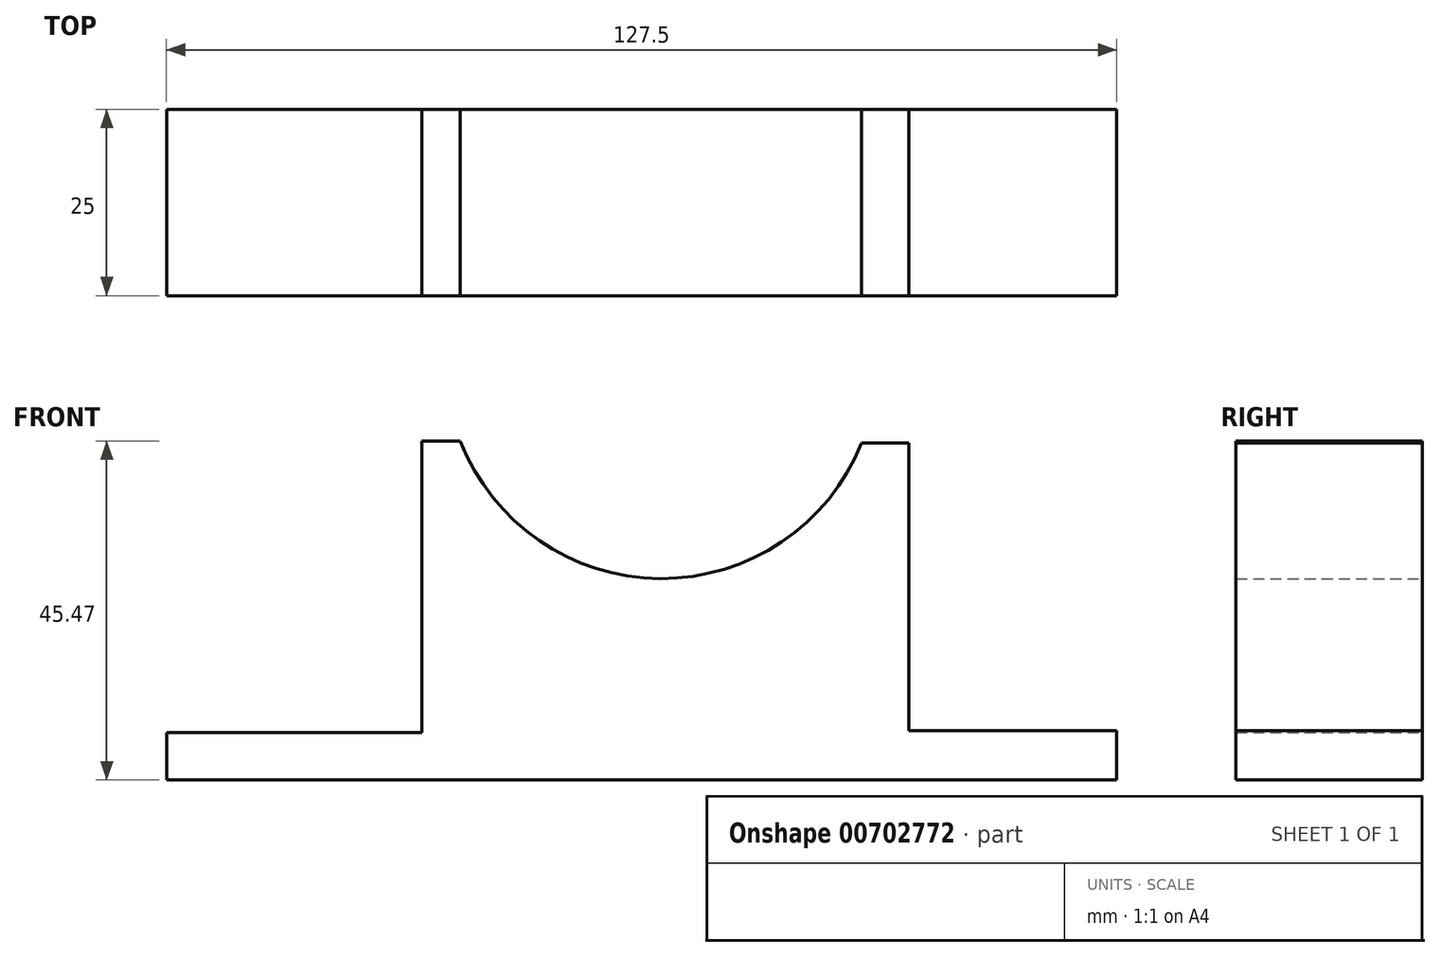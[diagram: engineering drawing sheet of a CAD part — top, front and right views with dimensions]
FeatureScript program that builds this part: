
annotation { "Feature Type Name" : "Feature", "Feature Type Description" : "" }
export const myFeature = defineFeature(function(context is Context, id is Id, definition is map)
    precondition{}
    {
        {
            var Q0;
            Q0=qCreatedBy(makeId("Front.planeOp"),FACE);
            var sketch = newSketch(context, id + "F0", { "sketchPlane" : qUnion([Q0])});
            skLineSegment(sketch, "E0", {"start": v(-62.89, -16.55) * mm, "end": v(-62.89, -22.88) * mm});
            skLineSegment(sketch, "E1", {"start": v(-62.89, -22.88) * mm, "end": v(64.61, -22.88) * mm});
            skLineSegment(sketch, "E2", {"start": v(64.61, -22.88) * mm, "end": v(64.61, -16.26) * mm});
            skLineSegment(sketch, "E3", {"start": v(64.61, -16.26) * mm, "end": v(36.7, -16.26) * mm});
            skLineSegment(sketch, "E4", {"start": v(-62.89, -16.55) * mm, "end": v(-28.64, -16.55) * mm});
            skLineSegment(sketch, "E5", {"start": v(-28.64, -16.55) * mm, "end": v(-28.64, 22.6) * mm});
            skLineSegment(sketch, "E6", {"start": v(-28.64, 22.6) * mm, "end": v(-23.46, 22.6) * mm});
            skLineSegment(sketch, "E7", {"start": v(36.7, -16.26) * mm, "end": v(36.7, 22.3) * mm});
            skLineSegment(sketch, "E8", {"start": v(36.7, 22.3) * mm, "end": v(30.36, 22.3) * mm});
            skArc(sketch, "E9", {"start": v(-23.46, 22.6) * mm, "mid": v(3.36, 4.13) * mm, "end": v(30.36, 22.3) * mm});
            skSolve(sketch);
        }
        {
            var Q0;
            Q0 = qSketchRegion(id + "F0", true);
            extrude(context, id + "F1", {"entities" : qUnion([Q0]), "depth" : 25 * mm, "offsetDistance" : 25 * mm});
        }
    });
